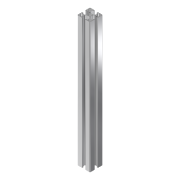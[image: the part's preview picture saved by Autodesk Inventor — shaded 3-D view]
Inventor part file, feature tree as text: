
AUTODESK INVENTOR PART (.ipt)
format: ipt  version: 2019 (Build 230136000, 136)  size: 308,224 bytes
history: native  units: mm
features: other x4, extrude x1, sketch x1, reference x1
ambient origin geometry x8: Origin, YZ Plane, XZ Plane, XY Plane, X Axis, Y Axis, Z Axis, Center Point
bodies: Body1 (feature_tree)
feature tree (7):
  other  "솔리드1"
  extrude  "돌출1"  Depth=305.0mm TaperAngle=0.0deg
  sketch  "스케치1"
  reference  "참조1"
  other  "<userpath>\Documents\Inventor\Projects\2019_CapstoneDesign\Body.iam"
  other  "Body.iam"
  other  "Propile_800:1"
